# Revit family: VENTS TT PRO
name_source: partatom
category: Mechanical Equipment
units: mm (PartAtom-declared; Revit-internal decimal feet)

## family parameters
Always vertical = No
Cut with Voids When Loaded = No
Part Type = Breaks Into
Room Calculation Point = No
Round Connector Dimension = Use Diameter
Shared = No
Work Plane-Based = No

## types (7) — shared parameters
CAT0 = Yes
CAT1 = Yes
CAT2 = Yes
Certification = by Manifacturer
Description = Inline mixed-flow fan
EC motor = No
Ingress Protection Rating = IPX4
LL7 = 98 mm  [stored 0.321522 ft]
Manufacturer = VENTS
Model = ТТ PRO
Motor IP Rating = IPX4
R3 = 49 mm  [stored 0.160761 ft]
RR4 = 12 mm  [stored 0.0393701 ft]
URL = https://ventilation-system.com
Variable Speed Drive = No
Voltage = 230 V
W = 500 mm
Угол = 60.00°
zero-valued in all types: Default Elevation

## per-type parameters (varying)
- TT PRO 160: Current.Max=0 A; Current.Min=0 A; D=160 mm; FlowMax=565.0 m³/h; FlowMin=415.0 m³/h; HH1=50 mm  [stored 0.164042 ft]; HH2=49 mm  [stored 0.160761 ft]; HH3=110 mm  [stored 0.360892 ft]; L8=82 mm  [stored 0.269029 ft]; LL1=145 mm; LL2=112 mm  [stored 0.367454 ft]; LL3=69 mm  [stored 0.226378 ft]; LL4=41 mm  [stored 0.134514 ft]; LL6=43 mm  [stored 0.141076 ft]; MC Product Code=ТТ PRO 160; Mass=3.25 kg; PC=134 mm; PE=115 mm  [stored 0.377297 ft]; Power max=50 W; Power min=42 W; R1=79 mm; R2=110 mm  [stored 0.360892 ft]; RR3=43 mm  [stored 0.141076 ft]; Service Zone=160 mm; Service Zone 1=240 mm; Service Zone 2=289 mm; Service zone=No; Sound Pressure Level at 3m  dBA (Min/Max)=32/44; WW1=70 mm  [stored 0.229659 ft]; WW2=52 mm
- TT PRO 200: Current.Max=0 A; Current.Min=0 A; D=200 mm; FlowMax=1040.0 m³/h; FlowMin=830.0 m³/h; HH1=50 mm  [stored 0.164042 ft]; HH2=49 mm  [stored 0.160761 ft]; HH3=120 mm  [stored 0.393701 ft]; L8=82 mm  [stored 0.269029 ft]; LL1=148 mm; LL2=115 mm  [stored 0.377297 ft]; LL3=70 mm  [stored 0.229659 ft]; LL4=41 mm  [stored 0.134514 ft]; LL6=43 mm  [stored 0.141076 ft]; MC Product Code=ТТ PRO 200; Mass=3.95 kg; PC=131 mm  [stored 0.42979 ft]; PE=130 mm  [stored 0.426509 ft]; Power max=108 W; Power min=76 W; R1=100 mm  [stored 0.328084 ft]; R2=120 mm  [stored 0.393701 ft]; RR3=43 mm  [stored 0.141076 ft]; Service Zone=170 mm; Service Zone 1=259 mm; Service Zone 2=296 mm; Service zone=No; Sound Pressure Level at 3m  dBA (Min/Max)=39/45; WW1=70 mm  [stored 0.229659 ft]; WW2=52 mm
- TT PRO 250: Current.Max=1 A; Current.Min=1 A; D=250 mm; FlowMax=1400.0 m³/h; FlowMin=1110.0 m³/h; HH1=50 mm  [stored 0.164042 ft]; HH2=49 mm  [stored 0.160761 ft]; HH3=144 mm; L8=108 mm  [stored 0.354331 ft]; LL1=192 mm; LL2=150 mm; LL3=119 mm  [stored 0.39042 ft]; LL4=54 mm  [stored 0.177165 ft]; LL6=89 mm; MC Product Code=ТТ PRO 250; Mass=7.80 kg; PC=170 mm; PE=153 mm; Power max=177 W; Power min=125 W; R1=123 mm  [stored 0.403543 ft]; R2=144 mm; RR3=50 mm  [stored 0.164042 ft]; Service Zone=194 mm; Service Zone 1=307 mm; Service Zone 2=383 mm; Service zone=Yes; Sound Pressure Level at 3m  dBA (Min/Max)=44/51; WW1=70 mm  [stored 0.229659 ft]; WW2=72 mm  [stored 0.23622 ft]
- TT PRO 315: Current.Max=1 A; Current.Min=1 A; D=315 mm; FlowMax=2050.0 m³/h; FlowMin=1570.0 m³/h; HH1=68 mm; HH2=132 mm  [stored 0.433071 ft]; HH3=181 mm; L8=108 mm  [stored 0.354331 ft]; LL1=223 mm; LL2=192 mm; LL3=155 mm; LL4=54 mm  [stored 0.177165 ft]; LL6=118 mm; MC Product Code=ТТ PRO 315; Mass=11.95 kg; PC=208 mm; PE=200 mm; Power max=320 W; Power min=230 W; R1=155 mm; R2=181 mm; RR3=50 mm  [stored 0.164042 ft]; Service Zone=231 mm; Service Zone 1=382 mm; Service Zone 2=445 mm; Service zone=Yes; Sound Pressure Level at 3m  dBA (Min/Max)=41/52; WW1=100 mm  [stored 0.328084 ft]; WW2=102 mm
- TT PRO 150: Current.Max=0 A; Current.Min=0 A; D=150 mm; FlowMax=565.0 m³/h; FlowMin=415.0 m³/h; HH1=68 mm; HH2=132 mm  [stored 0.433071 ft]; HH3=110 mm  [stored 0.360892 ft]; L8=108 mm  [stored 0.354331 ft]; LL1=145 mm; LL2=112 mm  [stored 0.367454 ft]; LL3=71 mm  [stored 0.23294 ft]; LL4=54 mm  [stored 0.177165 ft]; LL6=118 mm; MC Product Code=ТТ PRO 150; Mass=2.95 kg; PC=134 mm; PE=113 mm  [stored 0.370735 ft]; Power max=50 W; Power min=42 W; R1=74 mm  [stored 0.242782 ft]; R2=110 mm  [stored 0.360892 ft]; RR3=50 mm  [stored 0.164042 ft]; Service Zone=160 mm; Service Zone 1=240 mm; Service Zone 2=289 mm; Service zone=Yes; Sound Pressure Level at 3m  dBA (Min/Max)=32/44; WW1=56 mm  [stored 0.183727 ft]; WW2=58 mm  [stored 0.190289 ft]
- TT PRO 125: Current.Max=0 A; Current.Min=0 A; D=125 mm; FlowMax=350.0 m³/h; FlowMin=240.0 m³/h; HH1=50 mm  [stored 0.164042 ft]; HH2=49 mm  [stored 0.160761 ft]; HH3=98 mm  [stored 0.321522 ft]; L8=82 mm  [stored 0.269029 ft]; LL1=129 mm  [stored 0.423228 ft]; LL2=100 mm  [stored 0.328084 ft]; LL3=67 mm; LL4=41 mm  [stored 0.134514 ft]; LL6=43 mm  [stored 0.141076 ft]; MC Product Code=ТТ PRO 125; Mass=2.15 kg; PC=123 mm  [stored 0.403543 ft]; PE=103 mm  [stored 0.337927 ft]; Power max=29 W; Power min=25 W; R1=62 mm; R2=98 mm  [stored 0.321522 ft]; RR3=31 mm  [stored 0.101706 ft]; Service Zone=148 mm; Service Zone 1=216 mm; Service Zone 2=259 mm; Service zone=Yes; Sound Pressure Level at 3m  dBA (Min/Max)=29/34; WW1=50 mm  [stored 0.164042 ft]; WW2=52 mm
- TT PRO 100: Current.Max=0 A; Current.Min=0 A; D=100 mm; FlowMax=245.0 m³/h; FlowMin=180.0 m³/h; HH1=50 mm  [stored 0.164042 ft]; HH2=49 mm  [stored 0.160761 ft]; HH3=98 mm  [stored 0.321522 ft]; L8=82 mm  [stored 0.269029 ft]; LL1=151 mm; LL2=120 mm  [stored 0.393701 ft]; LL3=65 mm  [stored 0.213255 ft]; LL4=41 mm  [stored 0.134514 ft]; LL6=43 mm  [stored 0.141076 ft]; MC Product Code=ТТ PRO 100; Mass=1.75 kg; PC=123 mm  [stored 0.403543 ft]; PE=103 mm  [stored 0.337927 ft]; Power max=25 W; Power min=23 W; R1=49 mm  [stored 0.160761 ft]; R2=98 mm  [stored 0.321522 ft]; RR3=31 mm  [stored 0.101706 ft]; Service Zone=148 mm; Service Zone 1=216 mm; Service Zone 2=303 mm; Service zone=Yes; Sound Pressure Level at 3m  dBA (Min/Max)=27/32; WW1=50 mm  [stored 0.164042 ft]; WW2=52 mm

note: [stored X ft] marks values corroborated as IEEE doubles in the binary element streams (Revit-internal decimal feet)

## geometry (parser evidence)
native form markers: Sweep x1
no freeform markers — native parametric forms only
